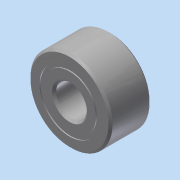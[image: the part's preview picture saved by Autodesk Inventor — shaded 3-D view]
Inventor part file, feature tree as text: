
AUTODESK INVENTOR PART (.ipt)
format: ipt  version: 2015 (Build 190159000, 159)  size: 608,256 bytes
history: native  units: in
note: dims shown in document units (in); Inventor stores cm internally (conversion verified against a paired STEP export)
features: imported_body x16, other x12, revolve x5
ambient origin geometry x8: Origin, YZ Plane, XZ Plane, XY Plane, X Axis, Y Axis, Z Axis, Center Point
bodies: Body1 (feature_tree), Body2 (feature_tree), Body3 (feature_tree), Body4 (feature_tree), Body5 (feature_tree), Body6 (feature_tree), Body7 (feature_tree), Body8 (feature_tree), Body9 (feature_tree), Body10 (feature_tree), Body11 (feature_tree), Body12 (feature_tree), Body13 (feature_tree), Body14 (feature_tree), Body15 (feature_tree), Body16 (feature_tree)
feature tree (33):
  revolve  "Revolve1"  [1 undecoded]
  other  "7804K1261"
  revolve  "Revolve3"  [1 undecoded]
  revolve  "Revolve4"  [1 undecoded]
  other  "CirPattern1[1]"
  other  "CirPattern1[2]"
  other  "CirPattern1[3]"
  other  "CirPattern1[4]"
  other  "CirPattern1[5]"
  other  "CirPattern1[6]"
  other  "CirPattern1[7]"
  other  "CirPattern1[8]"
  other  "CirPattern1[9]"
  other  "CirPattern1[10]"
  other  "CirPattern1[11]"
  revolve  "Revolve5[1]"  [1 undecoded]
  revolve  "Revolve5[2]"  [1 undecoded]
  imported_body  "Base1"
  imported_body  "Base2"
  imported_body  "Base3"
  imported_body  "Base4"
  imported_body  "Base5"
  imported_body  "Base6"
  imported_body  "Base7"
  imported_body  "Base8"
  imported_body  "Base9"
  imported_body  "Base10"
  imported_body  "Base11"
  imported_body  "Base12"
  imported_body  "Base13"
  imported_body  "Base14"
  imported_body  "Base15"
  imported_body  "Base16"
note: 5 required parameter values undecoded (feature->parameter linkage not recoverable at this tier; creation-order binding heuristic only, values carry confidence <= 0.55)
